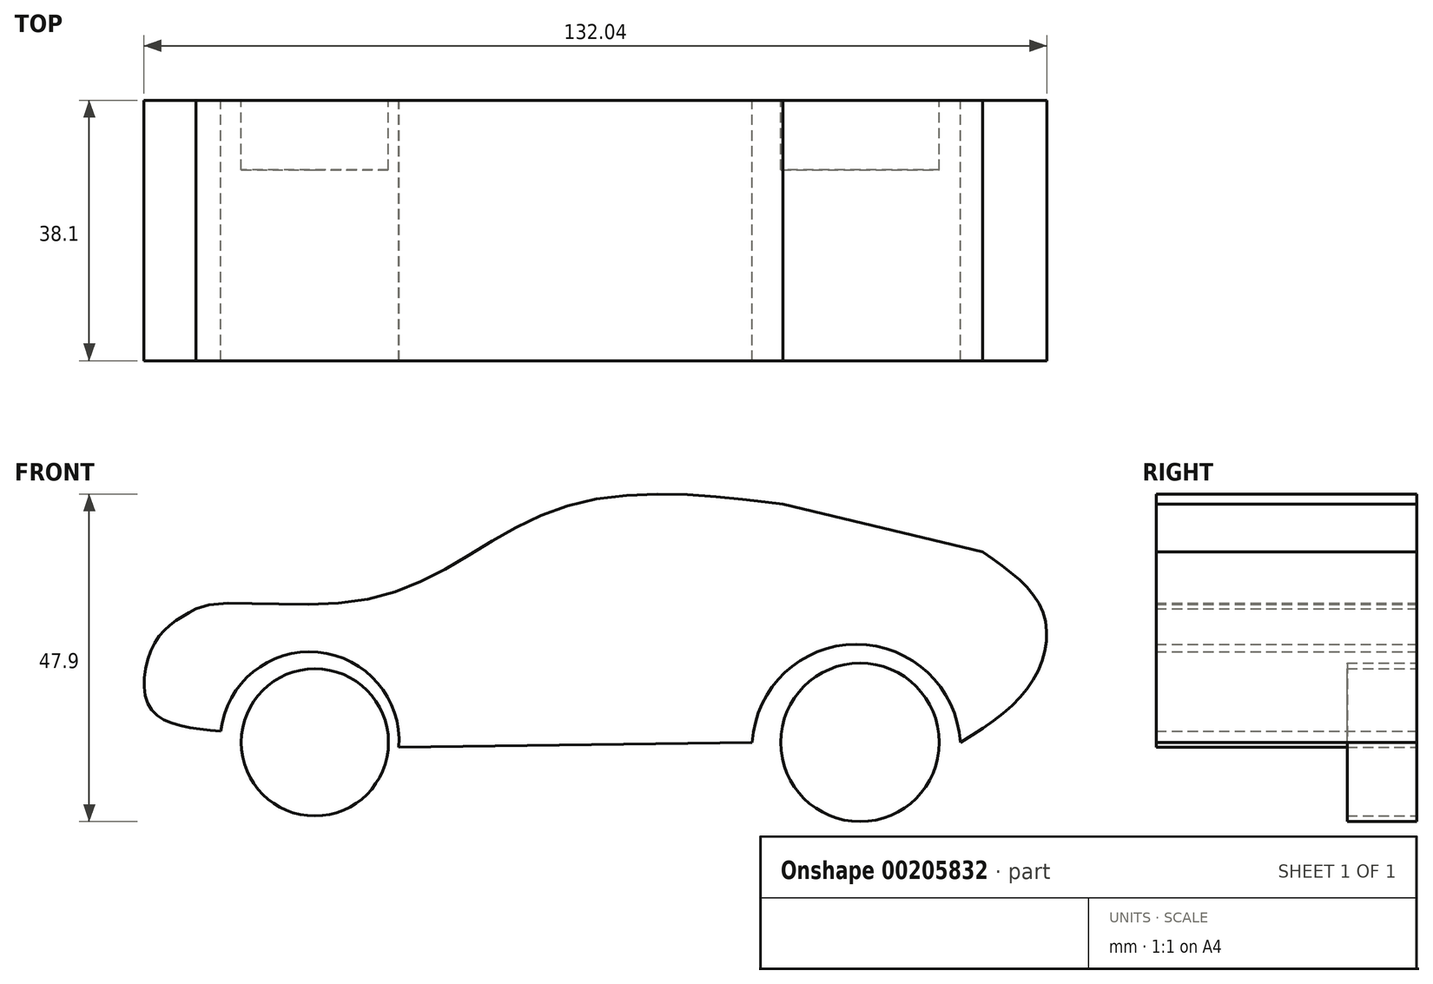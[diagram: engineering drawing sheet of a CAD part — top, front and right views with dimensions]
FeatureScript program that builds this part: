
annotation { "Feature Type Name" : "Feature", "Feature Type Description" : "" }
export const myFeature = defineFeature(function(context is Context, id is Id, definition is map)
    precondition{}
    {
        {
            var Q0;
            Q0=qCreatedBy(makeId("Front.planeOp"),FACE);
            var sketch = newSketch(context, id + "F0", { "sketchPlane" : qUnion([Q0])});
            skCircle(sketch, "E0", {"center": v(-49.86, -19.52) * mm, "radius": 10.76 * mm});
            skCircle(sketch, "E1", {"center": v(29.88, -19.52) * mm, "radius": 11.6 * mm});
            skSolve(sketch);
        }
        {
            var Q0;
            Q0=makeQuery(id+"F0.imprint","IMPRINT",FACE,{"disambiguationData":[TD([[makeQuery(id+"F0.imprint","IMPRINT",EDGE,{"derivedFrom":sQuery(id+"F0.wireOp",EDGE,"E0")}),1.0]])]});
            var Q1;
            Q1=makeQuery(id+"F0.imprint","IMPRINT",FACE,{"disambiguationData":[TD([[makeQuery(id+"F0.imprint","IMPRINT",EDGE,{"derivedFrom":sQuery(id+"F0.wireOp",EDGE,"E1")}),1.0]])]});
            extrude(context, id + "F1", {"entities" : qUnion([Q0, Q1]), "depth" : 10.16 * mm});
        }
        {
            var Q0;
            Q0=qCreatedBy(makeId("Front.planeOp"),FACE);
            var sketch = newSketch(context, id + "F2", { "sketchPlane" : qUnion([Q0])});
            skPoint(sketch, "E2.4.internal.orphan", {"position": v(61.59, 0) * mm});
            skPoint(sketch, "E2.endDerivative.orphan", {"position": v(56.46, 0) * mm});
            skPoint(sketch, "E3.start.orphan", {"position": v(67.27, 0) * mm});
            skFitSpline(sketch, "E4", {"points": [v(44.54, -19.52) * mm, v(55.54, -9.8) * mm, v(56.46, 0) * mm, v(47.84, 8.34) * mm], "startDerivative": vector(40.4, 23.61) * mm, "endDerivative": vector(-32.7, 23.03) * mm});
            skLineSegment(sketch, "E5", {"start": v(47.84, 8.34) * mm, "end": v(18.61, 15.3) * mm});
            skPoint(sketch, "E6.1.internal.orphan", {"position": v(-12.1, 15.3) * mm});
            skFitSpline(sketch, "E7", {"points": [v(18.61, 15.3) * mm, v(-12.1, 15.3) * mm, v(-41.43, 1.56) * mm, v(-67.27, 0) * mm], "startDerivative": vector(-52.02, 6.66) * mm, "endDerivative": vector(-31.65, -19.77) * mm});
            skPoint(sketch, "E8.end.orphan", {"position": v(-82.48, 0) * mm});
            skFitSpline(sketch, "E9", {"points": [v(-67.27, 0) * mm, v(-73.32, -5.04) * mm, v(-73.87, -14.57) * mm, v(-63.6, -17.87) * mm], "startDerivative": vector(-22.53, -12.3) * mm, "endDerivative": vector(35.73, -3.12) * mm});
            skArc(sketch, "E10", {"start": v(-37.58, -20.25) * mm, "mid": v(-49.42, -6.33) * mm, "end": v(-63.6, -17.87) * mm});
            skArc(sketch, "E11", {"start": v(44.54, -19.52) * mm, "mid": v(29.33, -5.17) * mm, "end": v(14.11, -19.52) * mm});
            skLineSegment(sketch, "E12", {"start": v(-37.58, -20.25) * mm, "end": v(14.11, -19.52) * mm});
            skSolve(sketch);
        }
        {
            var Q0;
            Q0=makeQuery(id+"F2.imprint","IMPRINT",FACE,{"disambiguationData":[TD([[makeQuery(id+"F2.imprint","IMPRINT",EDGE,{"derivedFrom":sQuery(id+"F2.wireOp",EDGE,"E4")}),1.0]])]});
            extrude(context, id + "F3", {"entities" : qUnion([Q0]), "depth" : 38.1 * mm});
        }
    });
